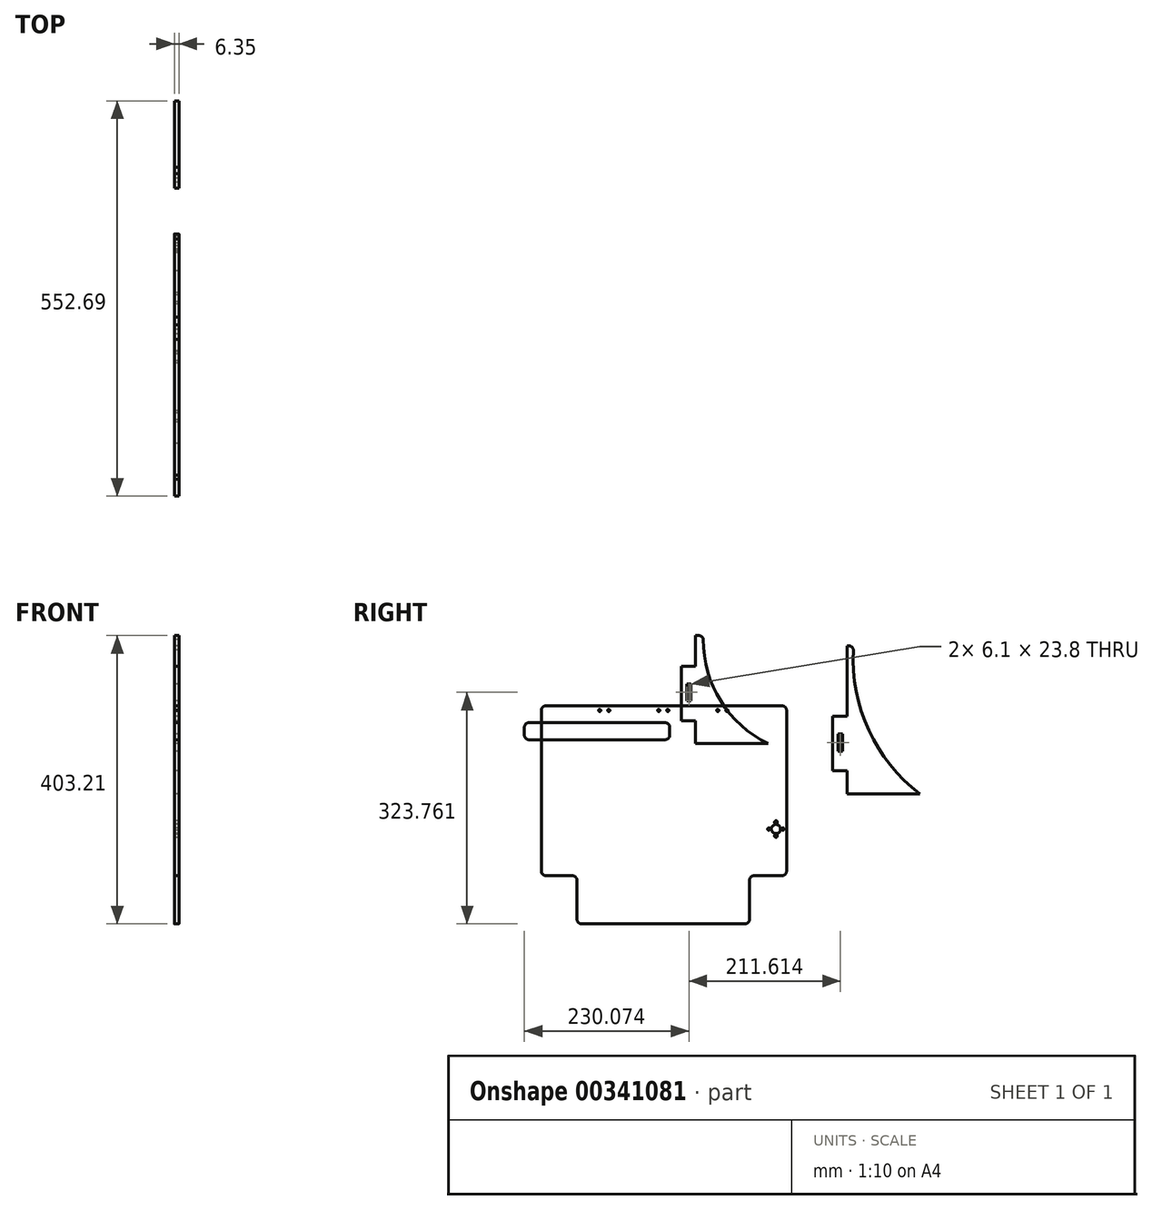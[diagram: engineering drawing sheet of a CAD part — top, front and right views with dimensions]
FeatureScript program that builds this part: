
annotation { "Feature Type Name" : "Feature", "Feature Type Description" : "" }
export const myFeature = defineFeature(function(context is Context, id is Id, definition is map)
    precondition{}
    {
        {
            var Q0;
            Q0=qCreatedBy(makeId("Right.planeOp"),FACE);
            var sketch = newSketch(context, id + "F0", { "sketchPlane" : qUnion([Q0])});
            skArc(sketch, "E0.filletArc", {"start": v(-180.43, 181.43) * mm, "mid": v(-184.26, 179.31) * mm, "end": v(-185.81, 175.22) * mm});
            skPoint(sketch, "E1.visualSharp", {"position": v(156.12, 58.24) * mm});
            skArc(sketch, "E1.filletArc", {"start": v(157.09, 175.15) * mm, "mid": v(154.87, 179.97) * mm, "end": v(149.77, 181.43) * mm});
            skPoint(sketch, "E2.orphan", {"position": v(156.12, 29.66) * mm});
            skArc(sketch, "E3.filletArc", {"start": v(111.67, -56.06) * mm, "mid": v(107.18, -57.92) * mm, "end": v(105.32, -62.41) * mm});
            skArc(sketch, "E4.filletArc", {"start": v(-135.98, -62.41) * mm, "mid": v(-137.84, -57.92) * mm, "end": v(-142.33, -56.06) * mm});
            skLineSegment(sketch, "E5", {"start": v(98.97, -123.37) * mm, "end": v(-129.63, -123.37) * mm});
            skPoint(sketch, "E6.visualSharp", {"position": v(105.32, -123.37) * mm});
            skArc(sketch, "E6.filletArc", {"start": v(98.97, -123.37) * mm, "mid": v(103.46, -121.51) * mm, "end": v(105.32, -117.02) * mm});
            skArc(sketch, "E7.filletArc", {"start": v(-135.98, -117.02) * mm, "mid": v(-134.12, -121.51) * mm, "end": v(-129.63, -123.37) * mm});
            skPoint(sketch, "E8.orphan", {"position": v(-185.9, 67.27) * mm});
            skLineSegment(sketch, "E9", {"start": v(-135.98, -62.41) * mm, "end": v(-135.98, -117.02) * mm});
            skLineSegment(sketch, "E10", {"start": v(105.32, -62.41) * mm, "end": v(105.32, -117.02) * mm});
            skLineSegment(sketch, "E11", {"start": v(-180.43, 181.43) * mm, "end": v(-15.33, 181.43) * mm});
            skLineSegment(sketch, "E12", {"start": v(-185.81, 175.22) * mm, "end": v(-185.81, -49.71) * mm});
            skLineSegment(sketch, "E13", {"start": v(-179.46, -56.06) * mm, "end": v(-142.33, -56.06) * mm});
            skLineSegment(sketch, "E14", {"start": v(111.67, -56.06) * mm, "end": v(150.74, -56.06) * mm});
            skLineSegment(sketch, "E15", {"start": v(157.09, -49.71) * mm, "end": v(157.09, 175.15) * mm});
            skPoint(sketch, "E16.visualSharp", {"position": v(-185.81, -56.06) * mm});
            skArc(sketch, "E16.filletArc", {"start": v(-185.81, -49.71) * mm, "mid": v(-183.95, -54.2) * mm, "end": v(-179.46, -56.06) * mm});
            skPoint(sketch, "E17.visualSharp", {"position": v(157.09, -56.06) * mm});
            skArc(sketch, "E17.filletArc", {"start": v(150.74, -56.06) * mm, "mid": v(155.23, -54.2) * mm, "end": v(157.09, -49.71) * mm});
            skPoint(sketch, "E18", {"position": v(-15.33, 181.43) * mm});
            skPoint(sketch, "E19", {"position": v(-97.88, 181.43) * mm});
            skLineSegment(sketch, "E20", {"start": v(149.77, 181.43) * mm, "end": v(-15.33, 181.43) * mm});
            skPoint(sketch, "E21", {"position": v(67.22, 181.43) * mm});
            skCircle(sketch, "E22", {"center": v(73.57, 175.08) * mm, "radius": 1.59 * mm});
            skCircle(sketch, "E23", {"center": v(60.87, 175.08) * mm, "radius": 1.59 * mm});
            skCircle(sketch, "E24", {"center": v(-21.68, 175.08) * mm, "radius": 1.59 * mm});
            skCircle(sketch, "E25", {"center": v(-8.98, 175.08) * mm, "radius": 1.59 * mm});
            skPoint(sketch, "E26.orphan", {"position": v(-15.33, 175.08) * mm});
            skCircle(sketch, "E27", {"center": v(-104.23, 175.08) * mm, "radius": 1.59 * mm});
            skCircle(sketch, "E28", {"center": v(-91.53, 175.08) * mm, "radius": 1.59 * mm});
            skCircle(sketch, "E29.0", {"center": v(142.28, 9.21) * mm, "radius": 6.36 * mm});
            skCircle(sketch, "E29.1", {"center": v(142.28, 18.74) * mm, "radius": 2.03 * mm});
            skCircle(sketch, "E29.2", {"center": v(152.06, 9.21) * mm, "radius": 1.78 * mm});
            skCircle(sketch, "E29.3", {"center": v(142.28, -0.31) * mm, "radius": 2.03 * mm});
            skCircle(sketch, "E29.4", {"center": v(132.5, 9.21) * mm, "radius": 1.78 * mm});
            skSolve(sketch);
        }
        {
            var Q0;
            Q0 = qSketchRegion(id + "F0", true);
            extrude(context, id + "F1", {"entities" : qUnion([Q0]), "depth" : 6.35 * mm});
        }
        {
            var Q0;
            Q0=qCreatedBy(makeId("Right.planeOp"),FACE);
            var sketch = newSketch(context, id + "F2", { "sketchPlane" : qUnion([Q0])});
            skPoint(sketch, "E30.visualSharp", {"position": v(40.13, 279.84) * mm});
            skLineSegment(sketch, "E31.bottom", {"start": v(29.97, 160.83) * mm, "end": v(9.77, 160.83) * mm});
            skLineSegment(sketch, "E31.top", {"start": v(29.97, 237.03) * mm, "end": v(9.77, 237.03) * mm});
            skLineSegment(sketch, "E31.right", {"start": v(9.77, 160.83) * mm, "end": v(9.77, 237.03) * mm});
            skLineSegment(sketch, "E32.trimOffspring", {"start": v(29.97, 237.03) * mm, "end": v(29.97, 279.84) * mm});
            skLineSegment(sketch, "E33.bottom", {"start": v(23.62, 212.3) * mm, "end": v(17.53, 212.3) * mm});
            skLineSegment(sketch, "E33.top", {"start": v(23.62, 188.5) * mm, "end": v(17.53, 188.5) * mm});
            skLineSegment(sketch, "E33.left", {"start": v(23.62, 212.3) * mm, "end": v(23.62, 188.5) * mm});
            skLineSegment(sketch, "E33.right", {"start": v(17.53, 212.3) * mm, "end": v(17.53, 188.5) * mm});
            skLineSegment(sketch, "E34", {"start": v(131.57, 128.8) * mm, "end": v(29.97, 128.8) * mm});
            skLineSegment(sketch, "E35", {"start": v(29.97, 128.8) * mm, "end": v(29.97, 154.2) * mm});
            skLineSegment(sketch, "E36", {"start": v(29.97, 279.84) * mm, "end": v(34.32, 279.84) * mm});
            skArc(sketch, "E37.filletArc", {"start": v(40.64, 274.14) * mm, "mid": v(38.58, 278.2) * mm, "end": v(34.32, 279.84) * mm});
            skPoint(sketch, "E38.start.orphan", {"position": v(131.57, 279.84) * mm});
            skPoint(sketch, "E39.start.orphan", {"position": v(131.57, 154.2) * mm});
            skLineSegment(sketch, "E40", {"start": v(29.97, 154.2) * mm, "end": v(29.97, 160.83) * mm});
            skArc(sketch, "E41", {"start": v(40.64, 274.14) * mm, "mid": v(64.96, 188.24) * mm, "end": v(131.57, 128.8) * mm});
            skSolve(sketch);
        }
        {
            var Q0;
            Q0 = qSketchRegion(id + "F2", true);
            extrude(context, id + "F3", {"entities" : qUnion([Q0]), "depth" : 6.35 * mm});
        }
        {
            var Q0;
            Q0=qCreatedBy(makeId("Right.planeOp"),FACE);
            var sketch = newSketch(context, id + "F4", { "sketchPlane" : qUnion([Q0])});
            skLineSegment(sketch, "E42.bottom", {"start": v(-203.15, 157.9) * mm, "end": v(-12.65, 157.9) * mm});
            skLineSegment(sketch, "E42.top", {"start": v(-203.15, 134.1) * mm, "end": v(-12.65, 134.1) * mm});
            skLineSegment(sketch, "E42.left", {"start": v(-209.5, 151.56) * mm, "end": v(-209.5, 140.46) * mm});
            skLineSegment(sketch, "E42.right", {"start": v(-6.3, 151.56) * mm, "end": v(-6.3, 140.46) * mm});
            skPoint(sketch, "E43.visualSharp", {"position": v(-209.5, 157.9) * mm});
            skArc(sketch, "E43.filletArc", {"start": v(-203.15, 157.9) * mm, "mid": v(-207.64, 156.05) * mm, "end": v(-209.5, 151.56) * mm});
            skPoint(sketch, "E44.visualSharp", {"position": v(-209.5, 134.1) * mm});
            skArc(sketch, "E44.filletArc", {"start": v(-209.5, 140.46) * mm, "mid": v(-207.64, 135.97) * mm, "end": v(-203.15, 134.1) * mm});
            skPoint(sketch, "E45.visualSharp", {"position": v(-6.3, 134.1) * mm});
            skArc(sketch, "E45.filletArc", {"start": v(-12.65, 134.1) * mm, "mid": v(-8.16, 135.97) * mm, "end": v(-6.3, 140.46) * mm});
            skPoint(sketch, "E46.visualSharp", {"position": v(-6.3, 157.9) * mm});
            skArc(sketch, "E46.filletArc", {"start": v(-6.3, 151.56) * mm, "mid": v(-8.16, 156.05) * mm, "end": v(-12.65, 157.9) * mm});
            skSolve(sketch);
        }
        {
            var Q0;
            Q0 = qSketchRegion(id + "F4", true);
            extrude(context, id + "F5", {"entities" : qUnion([Q0]), "depth" : 6.35 * mm});
        }
        {
            var Q0;
            Q0=qCreatedBy(makeId("Right.planeOp"),FACE);
            var sketch = newSketch(context, id + "F6", { "sketchPlane" : qUnion([Q0])});
            skLineSegment(sketch, "E47", {"start": v(241.59, 265.41) * mm, "end": v(241.59, 166.63) * mm});
            skPoint(sketch, "E48.visualSharp", {"position": v(250.13, 265.41) * mm});
            skLineSegment(sketch, "E49", {"start": v(241.59, 83.8) * mm, "end": v(241.59, 90.43) * mm});
            skLineSegment(sketch, "E50.bottom", {"start": v(241.59, 90.43) * mm, "end": v(221.38, 90.43) * mm});
            skLineSegment(sketch, "E50.top", {"start": v(241.59, 166.63) * mm, "end": v(221.38, 166.63) * mm});
            skLineSegment(sketch, "E50.right", {"start": v(221.38, 90.43) * mm, "end": v(221.38, 166.63) * mm});
            skLineSegment(sketch, "E51.bottom", {"start": v(235.24, 118.1) * mm, "end": v(229.14, 118.1) * mm});
            skLineSegment(sketch, "E51.top", {"start": v(235.24, 141.9) * mm, "end": v(229.14, 141.9) * mm});
            skLineSegment(sketch, "E51.left", {"start": v(235.24, 118.1) * mm, "end": v(235.24, 141.9) * mm});
            skLineSegment(sketch, "E51.right", {"start": v(229.14, 118.1) * mm, "end": v(229.14, 141.9) * mm});
            skLineSegment(sketch, "E52", {"start": v(343.19, 58.4) * mm, "end": v(241.59, 58.4) * mm});
            skLineSegment(sketch, "E53", {"start": v(241.59, 58.4) * mm, "end": v(241.59, 83.8) * mm});
            skLineSegment(sketch, "E54", {"start": v(244.13, 265.41) * mm, "end": v(241.59, 265.41) * mm});
            skLineSegment(sketch, "E55.trimOffspring", {"start": v(241.59, 90.43) * mm, "end": v(241.59, 83.8) * mm});
            skPoint(sketch, "E56.end.orphan", {"position": v(341.57, 265.41) * mm});
            skArc(sketch, "E57.filletArc", {"start": v(250.46, 259.48) * mm, "mid": v(248.47, 263.7) * mm, "end": v(244.13, 265.41) * mm});
            skArc(sketch, "E58", {"start": v(250.46, 259.48) * mm, "mid": v(271.97, 147.49) * mm, "end": v(343.19, 58.4) * mm});
            skSolve(sketch);
        }
        {
            var Q0;
            Q0 = qSketchRegion(id + "F6", true);
            extrude(context, id + "F7", {"entities" : qUnion([Q0]), "depth" : 6.35 * mm});
        }
    });
